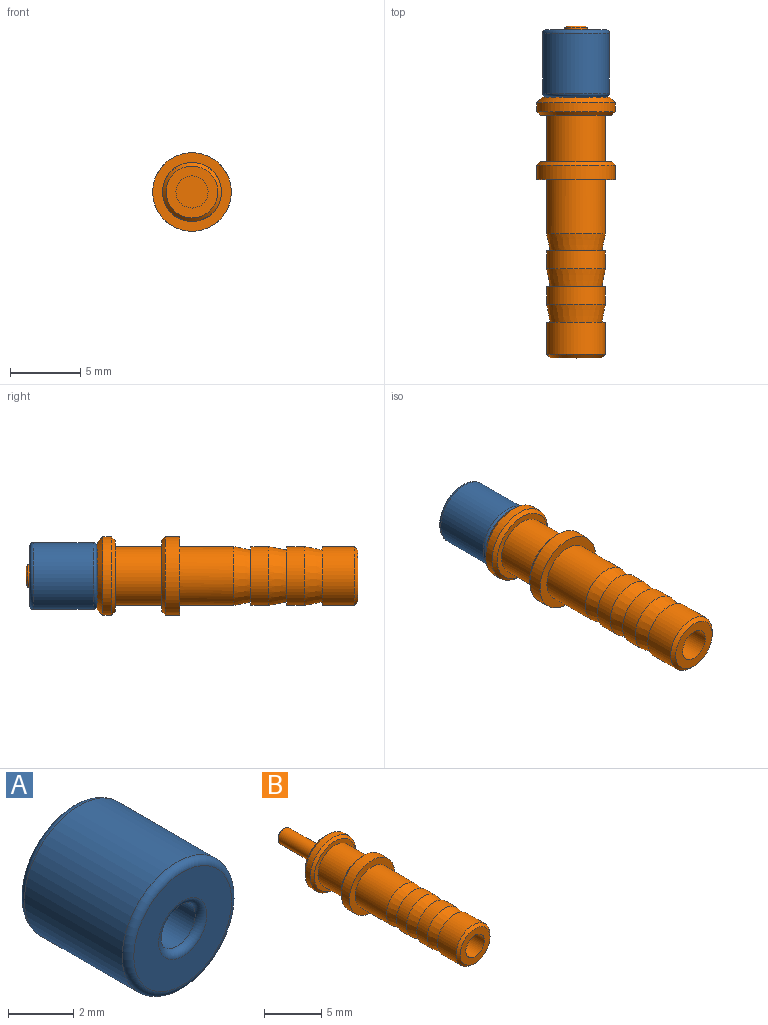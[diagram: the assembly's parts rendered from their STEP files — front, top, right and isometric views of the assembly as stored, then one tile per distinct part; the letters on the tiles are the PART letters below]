
ASSEMBLY  parts=2 mates=1
PART A: 8 faces, bbox 5.2x4.8x5.2 mm
  f0: cylinder r=0.79mm len=4.25mm, axis (0,-1,0), area 21.2mm2, adj f4,f7
  f1: cylinder r=2.38mm len=4.76mm, axis (0,-1,0), area 63.7mm2, adj f5,f6
  f2: plane 4.25x4.25mm, normal (0,1,0), area 10.8mm2, adj f5,f7
  f3: plane 4.25x4.25mm, normal (0,-1,0), area 10.8mm2, adj f4,f6
  f4: torus R=1.05mm, axis (0,1,0), area 2.2mm2, adj f0,f3
  f5: torus R=2.13mm, axis (0,1,0), area 5.7mm2, adj f1,f2
  f6: torus R=2.13mm, axis (0,1,0), area 5.7mm2, adj f1,f3
  f7: torus R=1.05mm, axis (0,1,0), area 2.2mm2, adj f0,f2
PART B: 28 faces, bbox 5.6x23.6x5.6 mm
  f0: cylinder r=2.79mm len=5.59mm, axis (0,1,0), area 11.1mm2, adj f6,f8
  f1: plane 1.35x1.35mm, normal (0,1,0), area 1.4mm2, adj f2
  f2: cone r=0.67mm half-angle=45deg, axis (0,-1,0), area 0.8mm2, adj f1,f3
  f3: cylinder r=0.8mm len=4.7mm, axis (0,-1,0), area 23.6mm2, adj f2,f4
  f4: torus R=1.05mm, axis (0,-1,0), area 2.2mm2, adj f3,f5
  f5: plane 4.83x4.83mm, normal (0,1,0), area 14.8mm2, adj f4,f6
  f6: cone r=2.79mm half-angle=45deg, axis (0,-1,0), area 8.8mm2, adj f0,f5
  f7: plane 5.08x5.08mm, normal (0,-1,0), area 6.5mm2, adj f8,f24
  f8: cone r=2.54mm half-angle=45deg, axis (0,1,0), area 6mm2, adj f0,f7
  f9: cylinder r=2.1mm len=4.19mm, axis (0,1,0), area 51mm2, adj f10,f23
  f10: cone r=1.84mm half-angle=11.9deg, axis (0,1,0), area 15.3mm2, adj f9,f11
  f11: plane 4.19x4.19mm, normal (0,1,0), area 3.1mm2, adj f10,f12
  f12: cylinder r=2.1mm len=4.19mm, axis (0,1,0), area 16.7mm2, adj f11,f14
  f13: plane 4.19x4.19mm, normal (0,1,0), area 3.1mm2, adj f14,f15
  f14: cone r=2.1mm half-angle=11.3deg, axis (0,1,0), area 16mm2, adj f12,f13
  f15: cylinder r=2.1mm len=4.19mm, axis (0,1,0), area 16.7mm2, adj f13,f16
  f16: cone r=2.1mm half-angle=11.3deg, axis (0,1,0), area 16mm2, adj f15,f17
  f17: plane 4.19x4.19mm, normal (0,1,0), area 3.1mm2, adj f16,f19
  f18: plane 3.68x3.68mm, normal (0,-1,0), area 6.6mm2, adj f20,f26
  f19: cylinder r=2.1mm len=4.19mm, axis (0,1,0), area 30.1mm2, adj f17,f20
  f20: cone r=1.84mm half-angle=45deg, axis (0,1,0), area 4.4mm2, adj f18,f19
  f21: cylinder r=2.79mm len=5.59mm, axis (0,-1,0), area 17.8mm2, adj f23,f25
  f22: plane 5.08x5.08mm, normal (0,1,0), area 6.5mm2, adj f24,f25
  f23: plane 5.59x5.59mm, normal (0,-1,0), area 10.7mm2, adj f9,f21
  f24: cylinder r=2.1mm len=4.19mm, axis (0,-1,0), area 43.5mm2, adj f7,f22
  f25: cone r=2.54mm half-angle=45deg, axis (0,-1,0), area 6mm2, adj f21,f22
  f26: cylinder r=1.14mm len=15.24mm, axis (0,-1,0), area 109.4mm2, adj f18,f27
  f27: plane 2.28x2.28mm, normal (0,-1,0), area 4.1mm2, adj f26
PLACE A rot(axis=(0,-1,0),2.3deg) t=(0,3.19,0)mm
PLACE B at identity fixed
MATE cylindrical B.f2 <-> A.f0  axis (0,-1,0) through (0,3.37,0)mm
